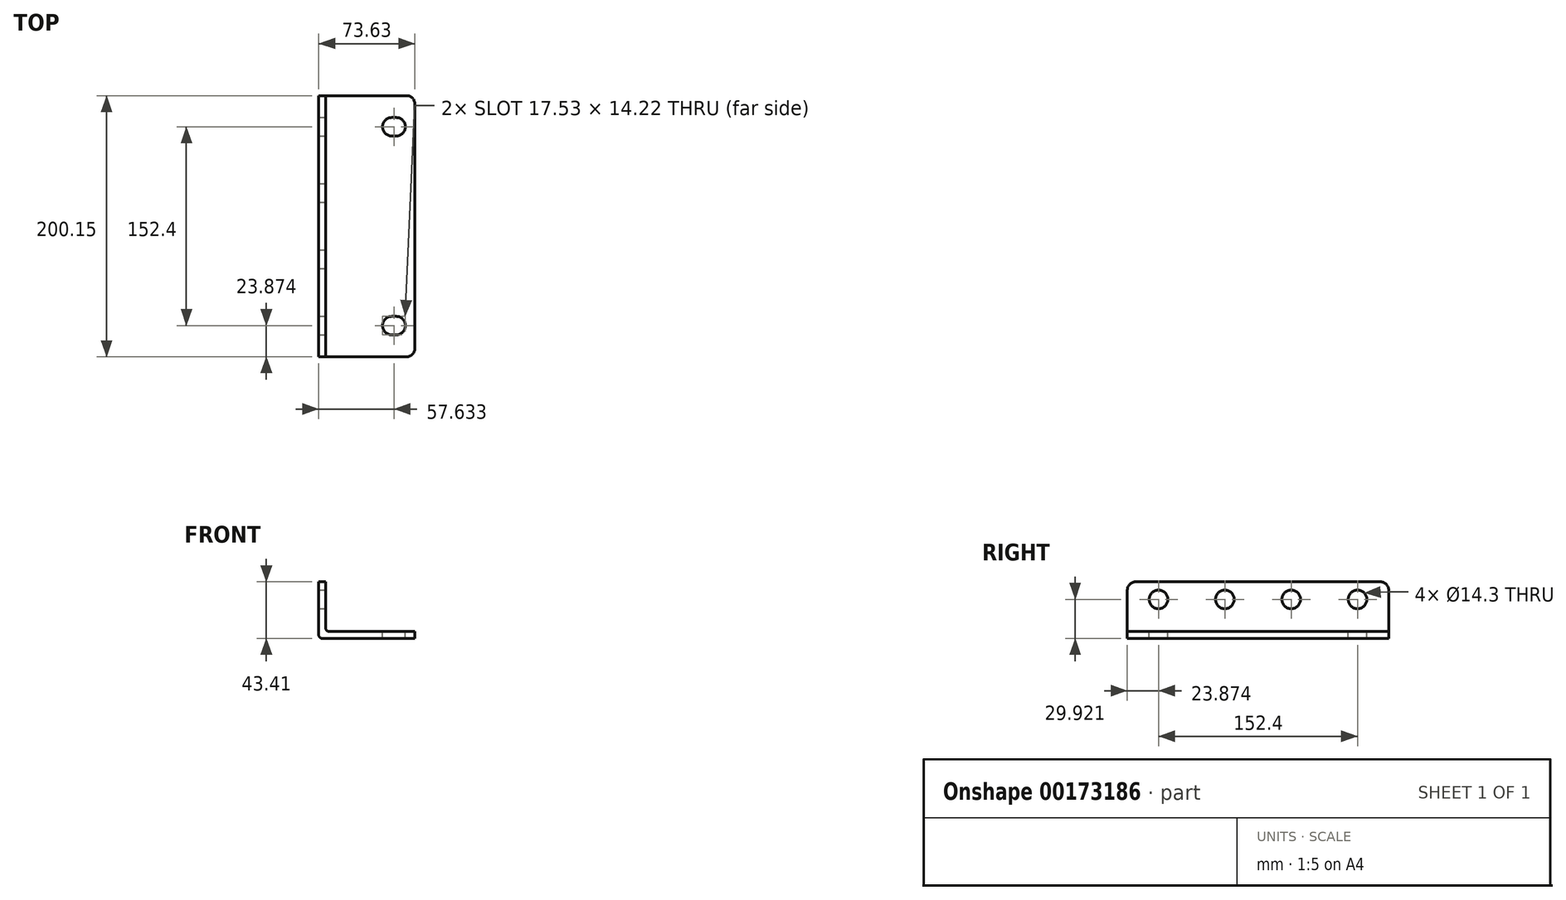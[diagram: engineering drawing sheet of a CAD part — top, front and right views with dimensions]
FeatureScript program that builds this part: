
annotation { "Feature Type Name" : "Feature", "Feature Type Description" : "" }
export const myFeature = defineFeature(function(context is Context, id is Id, definition is map)
    precondition{}
    {
        {
            var Q0;
            Q0=qCreatedBy(makeId("Front.planeOp"),FACE);
            var sketch = newSketch(context, id + "F0", { "sketchPlane" : qUnion([Q0])});
            skLineSegment(sketch, "E0", {"start": v(2.8, 0) * mm, "end": v(73.63, 0) * mm});
            skLineSegment(sketch, "E1", {"start": v(73.63, 0) * mm, "end": v(73.63, 5.3) * mm});
            skLineSegment(sketch, "E2", {"start": v(73.63, 5.3) * mm, "end": v(8.1, 5.3) * mm});
            skLineSegment(sketch, "E3", {"start": v(5.3, 8.1) * mm, "end": v(5.3, 43.4) * mm});
            skLineSegment(sketch, "E4", {"start": v(5.3, 43.4) * mm, "end": v(0, 43.4) * mm});
            skLineSegment(sketch, "E5", {"start": v(0, 43.4) * mm, "end": v(0, 2.8) * mm});
            skPoint(sketch, "E6.visualSharp", {"position": v(0, 0) * mm});
            skArc(sketch, "E6.filletArc", {"start": v(0, 2.8) * mm, "mid": v(0.82, 0.82) * mm, "end": v(2.8, 0) * mm});
            skPoint(sketch, "E7.visualSharp", {"position": v(5.3, 5.3) * mm});
            skArc(sketch, "E7.filletArc", {"start": v(5.3, 8.1) * mm, "mid": v(6.13, 6.13) * mm, "end": v(8.1, 5.3) * mm});
            skPoint(sketch, "E8.visualSharp", {"position": v(0, 43.4) * mm});
            skLineSegment(sketch, "E8.filletArc", {"start": v(0, 43.4) * mm, "end": v(0, 43.4) * mm});
            skPoint(sketch, "E9.visualSharp", {"position": v(73.63, 5.3) * mm});
            skLineSegment(sketch, "E9.filletArc", {"start": v(73.63, 5.3) * mm, "end": v(73.63, 5.3) * mm});
            skPoint(sketch, "E10.visualSharp", {"position": v(73.63, 0) * mm});
            skLineSegment(sketch, "E10.filletArc", {"start": v(73.63, 0) * mm, "end": v(73.63, 0) * mm});
            skPoint(sketch, "E11.visualSharp", {"position": v(5.3, 43.4) * mm});
            skLineSegment(sketch, "E11.filletArc", {"start": v(5.3, 43.4) * mm, "end": v(5.3, 43.4) * mm});
            skSolve(sketch);
        }
        {
            var Q0;
            Q0=makeQuery(id+"F0.imprint","IMPRINT",FACE,{"disambiguationData":[TD([[makeQuery(id+"F0.imprint","IMPRINT",EDGE,{"derivedFrom":sQuery(id+"F0.wireOp",EDGE,"E0")}),1.0]])]});
            extrude(context, id + "F1", {"entities" : qUnion([Q0]), "depth" : 200.15 * mm});
        }
        {
            var Q0;
            Q0=makeQuery(id+"F1.opExtrude","SWEPT_FACE",FACE,{"disambiguationData":[OSD([sQuery(id+"F0.wireOp",EDGE,"E5")])]});
            var sketch = newSketch(context, id + "F2", { "sketchPlane" : qUnion([Q0])});
            skPoint(sketch, "E12", {"position": v(176.28, 29.92) * mm});
            skPoint(sketch, "E13", {"position": v(125.48, 29.92) * mm});
            skPoint(sketch, "E14", {"position": v(74.68, 29.92) * mm});
            skPoint(sketch, "E15", {"position": v(23.88, 29.92) * mm});
            skSolve(sketch);
        }
        {
            var Q0;
            Q0=sQuery(id+"F2.wireOp",VERTEX,"E15");
            var Q1;
            Q1=sQuery(id+"F2.wireOp",VERTEX,"E14");
            var Q2;
            Q2=sQuery(id+"F2.wireOp",VERTEX,"E13");
            var Q3;
            Q3=sQuery(id+"F2.wireOp",VERTEX,"E12");
            var Q4;
            Q4=makeQuery(id+"F1.opExtrude","SWEPT_BODY",BODY,{"disambiguationData":[OSD([sQuery(id+"F0.wireOp",EDGE,"E0"),sQuery(id+"F0.wireOp",EDGE,"E1"),sQuery(id+"F0.wireOp",EDGE,"E2"),sQuery(id+"F0.wireOp",EDGE,"E3"),sQuery(id+"F0.wireOp",EDGE,"E4"),sQuery(id+"F0.wireOp",EDGE,"E5"),sQuery(id+"F0.wireOp",EDGE,"E6.filletArc"),sQuery(id+"F0.wireOp",EDGE,"E7.filletArc"),sQuery(id+"F0.wireOp",EDGE,"E8.filletArc"),sQuery(id+"F0.wireOp",EDGE,"E9.filletArc"),sQuery(id+"F0.wireOp",EDGE,"E10.filletArc"),sQuery(id+"F0.wireOp",EDGE,"E11.filletArc")])]});
            hole(context, id + "F3", {"style" : HoleStyle.SIMPLE, "endStyle" : HoleEndStyle.THROUGH, "holeDiameter" : 14.3 * mm, "locations" : qUnion([Q0, Q1, Q2, Q3]), "scope" : qUnion([Q4]), "isTappedThrough" : true});
        }
        {
            var Q0;
            Q0=makeQuery(id+"F1.opExtrude","CAP_EDGE",EDGE,{"disambiguationData":[OSD([sQuery(id+"F0.wireOp",EDGE,"E4")])],"isStart":true});
            var Q1;
            Q1=makeQuery(id+"F1.opExtrude","CAP_EDGE",EDGE,{"disambiguationData":[OSD([sQuery(id+"F0.wireOp",EDGE,"E1")])],"isStart":true});
            var Q2;
            Q2=makeQuery(id+"F1.opExtrude","CAP_EDGE",EDGE,{"disambiguationData":[OSD([sQuery(id+"F0.wireOp",EDGE,"E1")])],"isStart":false});
            var Q3;
            Q3=makeQuery(id+"F1.opExtrude","CAP_EDGE",EDGE,{"disambiguationData":[OSD([sQuery(id+"F0.wireOp",EDGE,"E4")])],"isStart":false});
            fillet(context, id + "F4", {"entities" : qUnion([Q0, Q1, Q2, Q3]), "radius" : 6.35 * mm, "tangentPropagation" : true, "allowEdgeOverflow" : false});
        }
        {
            var Q0;
            Q0=makeQuery(id+"F1.opExtrude","SWEPT_FACE",FACE,{"disambiguationData":[OSD([sQuery(id+"F0.wireOp",EDGE,"E2")])]});
            var sketch = newSketch(context, id + "F5", { "sketchPlane" : qUnion([Q0])});
            skPoint(sketch, "E16", {"position": v(57.63, -176.28) * mm});
            skPoint(sketch, "E17", {"position": v(57.63, -23.88) * mm});
            skLineSegment(sketch, "E18.bottom", {"start": v(59.28, -16.76) * mm, "end": v(55.98, -16.76) * mm});
            skLineSegment(sketch, "E18.top", {"start": v(59.28, -30.99) * mm, "end": v(55.98, -30.99) * mm});
            skLineSegment(sketch, "E18.left", {"start": v(66.4, -23.88) * mm, "end": v(66.4, -23.88) * mm});
            skLineSegment(sketch, "E18.right", {"start": v(48.87, -23.88) * mm, "end": v(48.87, -23.88) * mm});
            skLineSegment(sketch, "E19.bottom", {"start": v(59.28, -169.16) * mm, "end": v(55.98, -169.16) * mm});
            skLineSegment(sketch, "E19.top", {"start": v(59.28, -183.39) * mm, "end": v(55.98, -183.39) * mm});
            skLineSegment(sketch, "E19.left", {"start": v(66.4, -176.28) * mm, "end": v(66.4, -176.28) * mm});
            skLineSegment(sketch, "E19.right", {"start": v(48.87, -176.28) * mm, "end": v(48.87, -176.28) * mm});
            skPoint(sketch, "E20.visualSharp", {"position": v(66.4, -16.76) * mm});
            skArc(sketch, "E20.filletArc", {"start": v(66.4, -23.88) * mm, "mid": v(64.31, -18.85) * mm, "end": v(59.28, -16.76) * mm});
            skPoint(sketch, "E21.visualSharp", {"position": v(66.4, -30.99) * mm});
            skArc(sketch, "E21.filletArc", {"start": v(59.28, -30.99) * mm, "mid": v(64.31, -28.9) * mm, "end": v(66.4, -23.88) * mm});
            skPoint(sketch, "E22.visualSharp", {"position": v(48.87, -30.99) * mm});
            skArc(sketch, "E22.filletArc", {"start": v(48.87, -23.88) * mm, "mid": v(50.95, -28.9) * mm, "end": v(55.98, -30.99) * mm});
            skPoint(sketch, "E23.visualSharp", {"position": v(48.87, -16.76) * mm});
            skArc(sketch, "E23.filletArc", {"start": v(55.98, -16.76) * mm, "mid": v(50.95, -18.85) * mm, "end": v(48.87, -23.88) * mm});
            skPoint(sketch, "E24.visualSharp", {"position": v(66.4, -169.16) * mm});
            skArc(sketch, "E24.filletArc", {"start": v(66.4, -176.28) * mm, "mid": v(64.31, -171.25) * mm, "end": v(59.28, -169.16) * mm});
            skPoint(sketch, "E25.visualSharp", {"position": v(66.4, -183.39) * mm});
            skArc(sketch, "E25.filletArc", {"start": v(59.28, -183.39) * mm, "mid": v(64.31, -181.3) * mm, "end": v(66.4, -176.28) * mm});
            skPoint(sketch, "E26.visualSharp", {"position": v(48.87, -183.39) * mm});
            skArc(sketch, "E26.filletArc", {"start": v(48.87, -176.28) * mm, "mid": v(50.95, -181.3) * mm, "end": v(55.98, -183.39) * mm});
            skPoint(sketch, "E27.visualSharp", {"position": v(48.87, -169.16) * mm});
            skArc(sketch, "E27.filletArc", {"start": v(55.98, -169.16) * mm, "mid": v(50.95, -171.25) * mm, "end": v(48.87, -176.28) * mm});
            skSolve(sketch);
        }
        {
            var Q0;
            Q0=makeQuery(id+"F5.imprint","IMPRINT",FACE,{"disambiguationData":[TD([[makeQuery(id+"F5.imprint","IMPRINT",EDGE,{"derivedFrom":sQuery(id+"F5.wireOp",EDGE,"E18.bottom")}),1.0]])]});
            var Q1;
            Q1=makeQuery(id+"F5.imprint","IMPRINT",FACE,{"disambiguationData":[TD([[makeQuery(id+"F5.imprint","IMPRINT",EDGE,{"derivedFrom":sQuery(id+"F5.wireOp",EDGE,"E19.bottom")}),1.0]])]});
            extrude(context, id + "F6", {"entities" : qUnion([Q0, Q1]), "operationType" : NewBodyOperationType.REMOVE, "oppositeDirection" : true, "depth" : 25.4 * mm});
        }
    });
